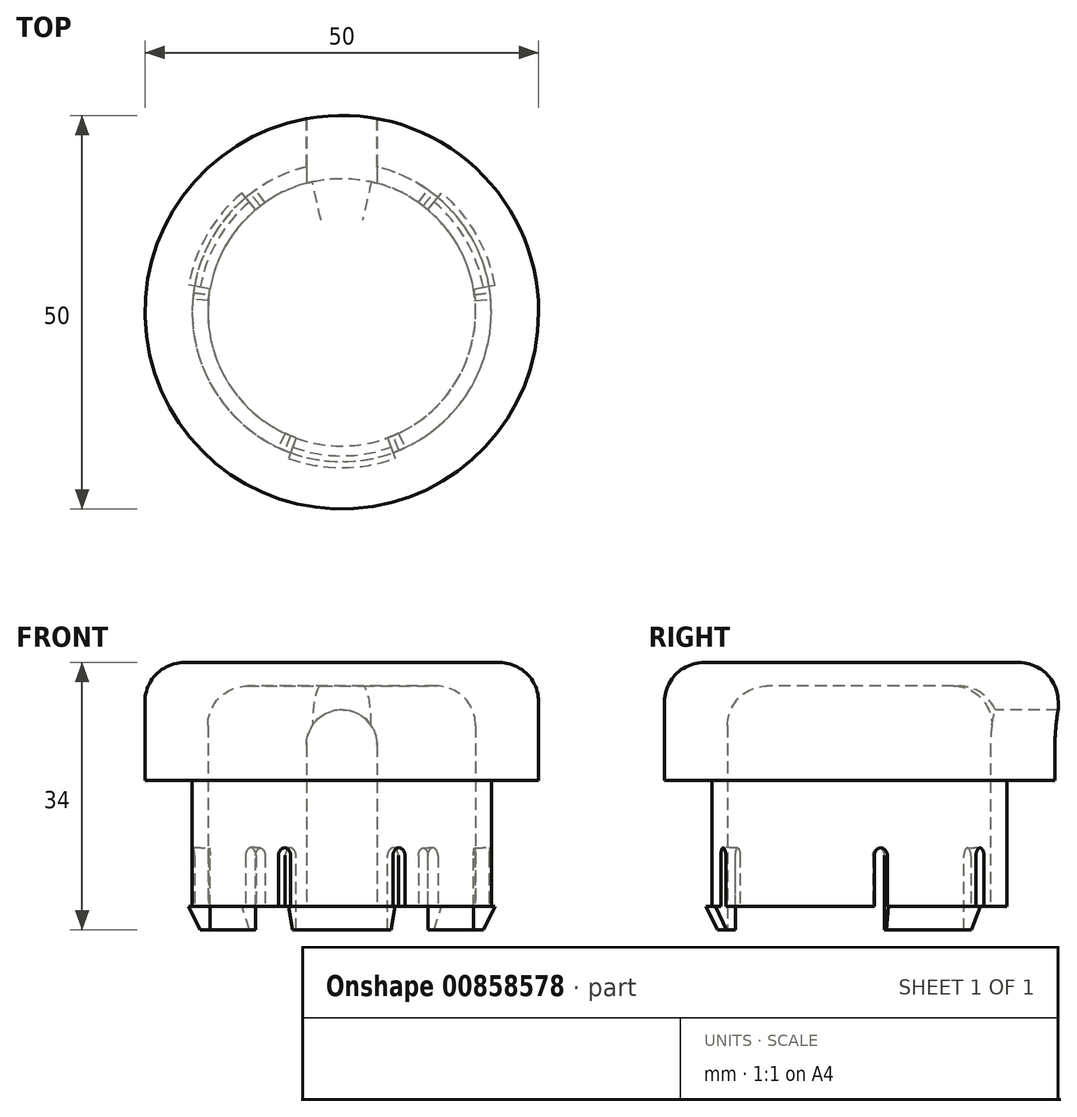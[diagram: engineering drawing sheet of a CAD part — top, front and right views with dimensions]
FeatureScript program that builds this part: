
annotation { "Feature Type Name" : "Feature", "Feature Type Description" : "" }
export const myFeature = defineFeature(function(context is Context, id is Id, definition is map)
    precondition{}
    {
        {
            var Q0;
            Q0=qCreatedBy(makeId("Top.planeOp"),FACE);
            var sketch = newSketch(context, id + "F0", { "sketchPlane" : qUnion([Q0])});
            skCircle(sketch, "E0", {"center": v(0, 0) * mm, "radius": 19 * mm});
            skSolve(sketch);
        }
        {
            var Q0;
            Q0 = qSketchRegion(id + "F0", true);
            extrude(context, id + "F1", {"entities" : qUnion([Q0]), "depth" : 16 * mm, "offsetDistance" : 25 * mm});
        }
        {
            var Q0;
            Q0=makeQuery(id+"F1.opExtrude","CAP_FACE",FACE,{"disambiguationData":[OSD([sQuery(id+"F0.wireOp",EDGE,"E0")])],"isStart":false});
            var sketch = newSketch(context, id + "F2", { "sketchPlane" : qUnion([Q0])});
            skCircle(sketch, "E1", {"center": v(0, 0) * mm, "radius": 25 * mm});
            skSolve(sketch);
        }
        {
            var Q0;
            Q0 = qSketchRegion(id + "F2", true);
            extrude(context, id + "F3", {"entities" : qUnion([Q0]), "operationType" : NewBodyOperationType.ADD, "depth" : 15 * mm, "offsetDistance" : 25 * mm});
        }
        {
            var Q0;
            Q0=makeQuery(id+"F1.opExtrude","CAP_FACE",FACE,{"disambiguationData":[OSD([sQuery(id+"F0.wireOp",EDGE,"E0")])],"isStart":true});
            var sketch = newSketch(context, id + "F4", { "sketchPlane" : qUnion([Q0])});
            skCircle(sketch, "E2", {"center": v(0, 0) * mm, "radius": 17 * mm});
            skSolve(sketch);
        }
        {
            var Q0;
            Q0 = qSketchRegion(id + "F4", true);
            extrude(context, id + "F5", {"entities" : qUnion([Q0]), "operationType" : NewBodyOperationType.REMOVE, "oppositeDirection" : true, "depth" : 28 * mm, "offsetDistance" : 25 * mm});
        }
        {
            var Q0;
            Q0=qCreatedBy(makeId("Front.planeOp"),FACE);
            var sketch = newSketch(context, id + "F6", { "sketchPlane" : qUnion([Q0])});
            skLineSegment(sketch, "E3", {"start": v(-4.5, 0) * mm, "end": v(-4.5, 20.5) * mm});
            skLineSegment(sketch, "E4", {"start": v(-8.7, 16) * mm, "end": v(8.8, 16) * mm});
            skLineSegment(sketch, "E5.0", {"start": v(-8.7, 25) * mm, "end": v(8.8, 25) * mm});
            skLineSegment(sketch, "E6.MirrorCS", {"start": v(4.5, 0) * mm, "end": v(4.5, 20.5) * mm});
            skArc(sketch, "E7", {"start": v(4.5, 20.5) * mm, "mid": v(0, 25) * mm, "end": v(-4.5, 20.5) * mm});
            skLineSegment(sketch, "E8", {"start": v(-4.5, 0) * mm, "end": v(4.5, 0) * mm});
            skSolve(sketch);
        }
        {
            var Q0;
            Q0 = qSketchRegion(id + "F6", true);
            extrude(context, id + "F7", {"entities" : qUnion([Q0]), "operationType" : NewBodyOperationType.REMOVE, "oppositeDirection" : true, "depth" : 25 * mm, "offsetDistance" : 25 * mm});
        }
        {
            var Q0;
            Q0=makeQuery(id+"F5.boolean.opBoolean","COPY",EDGE,{"derivedFrom":makeQuery(id+"F5.opExtrude","CAP_EDGE",EDGE,{"disambiguationData":[OSD([sQuery(id+"F4.wireOp",EDGE,"E2")])],"isStart":false})});
            fillet(context, id + "F8", {"entities" : qUnion([Q0]), "tangentPropagation" : true, "radius" : 5 * mm, "defaultsChanged" : false, "vertexSettings" : [], "allowEdgeOverflow" : false});
        }
        {
            var Q0;
            Q0=makeQuery(id+"F3.opExtrude","CAP_FACE",FACE,{"disambiguationData":[OSD([sQuery(id+"F2.wireOp",EDGE,"E1")])],"isStart":false});
            fillet(context, id + "F9", {"entities" : qUnion([Q0]), "tangentPropagation" : true, "radius" : 5 * mm, "defaultsChanged" : true, "vertexSettings" : [], "allowEdgeOverflow" : false});
        }
        {
            var Q0;
            Q0=makeQuery(id+"F1.opExtrude","CAP_FACE",FACE,{"disambiguationData":[OSD([sQuery(id+"F0.wireOp",EDGE,"E0")])],"isStart":true});
            var sketch = newSketch(context, id + "F10", { "sketchPlane" : qUnion([Q0])});
            skLineSegment(sketch, "E9", {"start": v(-5.81, 15.97) * mm, "end": v(-6.75, 18.56) * mm});
            skLineSegment(sketch, "E10.MirrorCS", {"start": v(5.81, 15.97) * mm, "end": v(6.75, 18.56) * mm});
            skArc(sketch, "E11", {"start": v(6.75, 18.56) * mm, "mid": v(0, 19.75) * mm, "end": v(-6.75, 18.56) * mm});
            skArc(sketch, "E12", {"start": v(5.81, 15.97) * mm, "mid": v(0, 17) * mm, "end": v(-5.81, 15.97) * mm});
            skArc(sketch, "E13.1.0", {"start": v(-19.45, -3.43) * mm, "mid": v(-17.1, -9.87) * mm, "end": v(-12.7, -15.13) * mm});
            skLineSegment(sketch, "E13.1.1", {"start": v(-10.93, -13.02) * mm, "end": v(-12.7, -15.13) * mm});
            skLineSegment(sketch, "E13.1.2", {"start": v(-16.74, -2.95) * mm, "end": v(-19.45, -3.43) * mm});
            skArc(sketch, "E13.1.3", {"start": v(-16.74, -2.95) * mm, "mid": v(-14.72, -8.5) * mm, "end": v(-10.93, -13.02) * mm});
            skArc(sketch, "E13.2.0", {"start": v(12.7, -15.13) * mm, "mid": v(17.1, -9.88) * mm, "end": v(19.45, -3.43) * mm});
            skLineSegment(sketch, "E13.2.1", {"start": v(16.74, -2.95) * mm, "end": v(19.45, -3.43) * mm});
            skLineSegment(sketch, "E13.2.2", {"start": v(10.93, -13.02) * mm, "end": v(12.7, -15.13) * mm});
            skArc(sketch, "E13.2.3", {"start": v(10.93, -13.02) * mm, "mid": v(14.72, -8.5) * mm, "end": v(16.74, -2.95) * mm});
            skSolve(sketch);
        }
        {
            var Q0;
            Q0 = qSketchRegion(id + "F10", true);
            extrude(context, id + "F11", {"entities" : qUnion([Q0]), "operationType" : NewBodyOperationType.ADD, "depth" : 3 * mm, "offsetDistance" : 25 * mm});
        }
        {
            var Q0;
            Q0=makeQuery(id+"F11.opExtrude","CAP_EDGE",EDGE,{"disambiguationData":[OSD([sQuery(id+"F10.wireOp",EDGE,"E13.1.0")])],"isStart":false});
            var Q1;
            Q1=makeQuery(id+"F11.opExtrude","CAP_EDGE",EDGE,{"disambiguationData":[OSD([sQuery(id+"F10.wireOp",EDGE,"E13.2.0")])],"isStart":false});
            var Q2;
            Q2=makeQuery(id+"F11.opExtrude","CAP_EDGE",EDGE,{"disambiguationData":[OSD([sQuery(id+"F10.wireOp",EDGE,"E11")])],"isStart":false});
            chamfer(context, id + "F12", {"entities" : qUnion([Q0, Q1, Q2]), "chamferType" : ChamferType.TWO_OFFSETS, "width1" : 1.5 * mm, "oppositeDirection" : false, "width2" : 3 * mm, "tangentPropagation" : true});
        }
        {
            var Q0;
            {var subQ0=sQuery(id+"F10.wireOp",EDGE,"E9");var subQ3=sQuery(id+"F0.wireOp",EDGE,"E0");Q0=makeQuery(id+"F11.boolean.opBoolean","SPLIT",FACE,{"disambiguationData":[TD([makeQuery(id+"F11.opExtrude","SWEPT_FACE",FACE,{"disambiguationData":[OSD([subQ0])]})])],"derivedFrom":makeQuery(id+"F1.opExtrude","CAP_FACE",FACE,{"disambiguationData":[OSD([subQ3])],"isStart":true})});}
            var sketch = newSketch(context, id + "F13", { "sketchPlane" : qUnion([Q0])});
            skLineSegment(sketch, "E14", {"start": v(-5.81, 15.97) * mm, "end": v(-6.5, 17.85) * mm});
            skLineSegment(sketch, "E15", {"start": v(-7.18, 15.4) * mm, "end": v(-8.03, 17.22) * mm});
            skArc(sketch, "E16", {"start": v(-5.81, 15.97) * mm, "mid": v(-6.5, 15.7) * mm, "end": v(-7.18, 15.4) * mm});
            skArc(sketch, "E17", {"start": v(-6.5, 17.85) * mm, "mid": v(-7.27, 17.55) * mm, "end": v(-8.03, 17.22) * mm});
            skArc(sketch, "E18.MirrorCS", {"start": v(5.81, 15.97) * mm, "mid": v(6.5, 15.7) * mm, "end": v(7.18, 15.4) * mm});
            skArc(sketch, "E19.MirrorCS", {"start": v(6.5, 17.85) * mm, "mid": v(7.27, 17.55) * mm, "end": v(8.03, 17.22) * mm});
            skLineSegment(sketch, "E20.MirrorCS", {"start": v(7.18, 15.4) * mm, "end": v(8.03, 17.22) * mm});
            skLineSegment(sketch, "E21.MirrorCS", {"start": v(5.81, 15.97) * mm, "end": v(6.5, 17.85) * mm});
            skLineSegment(sketch, "E22.1.0", {"start": v(-10.93, -13.02) * mm, "end": v(-12.21, -14.55) * mm});
            skLineSegment(sketch, "E22.1.1", {"start": v(-16.94, -1.48) * mm, "end": v(-18.93, -1.66) * mm});
            skLineSegment(sketch, "E22.1.2", {"start": v(-16.74, -2.95) * mm, "end": v(-18.71, -3.3) * mm});
            skLineSegment(sketch, "E22.1.3", {"start": v(-9.75, -13.93) * mm, "end": v(-10.9, -15.56) * mm});
            skArc(sketch, "E22.1.4", {"start": v(-10.93, -13.02) * mm, "mid": v(-10.35, -13.49) * mm, "end": v(-9.75, -13.93) * mm});
            skArc(sketch, "E22.1.5", {"start": v(-18.71, -3.3) * mm, "mid": v(-18.84, -2.48) * mm, "end": v(-18.93, -1.66) * mm});
            skArc(sketch, "E22.1.6", {"start": v(-12.21, -14.55) * mm, "mid": v(-11.57, -15.07) * mm, "end": v(-10.9, -15.56) * mm});
            skArc(sketch, "E22.1.7", {"start": v(-16.74, -2.95) * mm, "mid": v(-16.85, -2.22) * mm, "end": v(-16.94, -1.48) * mm});
            skLineSegment(sketch, "E22.2.0", {"start": v(16.74, -2.95) * mm, "end": v(18.71, -3.3) * mm});
            skLineSegment(sketch, "E22.2.1", {"start": v(9.75, -13.93) * mm, "end": v(10.9, -15.56) * mm});
            skLineSegment(sketch, "E22.2.2", {"start": v(10.93, -13.02) * mm, "end": v(12.21, -14.55) * mm});
            skLineSegment(sketch, "E22.2.3", {"start": v(16.94, -1.48) * mm, "end": v(18.93, -1.66) * mm});
            skArc(sketch, "E22.2.4", {"start": v(16.74, -2.95) * mm, "mid": v(16.85, -2.22) * mm, "end": v(16.94, -1.48) * mm});
            skArc(sketch, "E22.2.5", {"start": v(12.21, -14.55) * mm, "mid": v(11.57, -15.07) * mm, "end": v(10.9, -15.56) * mm});
            skArc(sketch, "E22.2.6", {"start": v(18.71, -3.3) * mm, "mid": v(18.84, -2.48) * mm, "end": v(18.93, -1.66) * mm});
            skArc(sketch, "E22.2.7", {"start": v(10.93, -13.02) * mm, "mid": v(10.35, -13.49) * mm, "end": v(9.75, -13.93) * mm});
            skSolve(sketch);
        }
        {
            var Q0;
            Q0 = qSketchRegion(id + "F13", true);
            extrude(context, id + "F14", {"entities" : qUnion([Q0]), "operationType" : NewBodyOperationType.REMOVE, "oppositeDirection" : true, "depth" : 7.5 * mm, "offsetDistance" : 25 * mm});
        }
        {
            var Q0;
            Q0=makeQuery(id+"F14.boolean.opBoolean","COPY",EDGE,{"derivedFrom":makeQuery(id+"F14.opExtrude","CAP_EDGE",EDGE,{"disambiguationData":[OSD([sQuery(id+"F13.wireOp",EDGE,"E22.2.2")])],"isStart":false})});
            var Q1;
            Q1=makeQuery(id+"F14.boolean.opBoolean","COPY",EDGE,{"derivedFrom":makeQuery(id+"F14.opExtrude","CAP_EDGE",EDGE,{"disambiguationData":[OSD([sQuery(id+"F13.wireOp",EDGE,"E22.2.1")])],"isStart":false})});
            var Q2;
            Q2=makeQuery(id+"F14.boolean.opBoolean","COPY",EDGE,{"derivedFrom":makeQuery(id+"F14.opExtrude","CAP_EDGE",EDGE,{"disambiguationData":[OSD([sQuery(id+"F13.wireOp",EDGE,"E22.2.0")])],"isStart":false})});
            var Q3;
            Q3=makeQuery(id+"F14.boolean.opBoolean","COPY",EDGE,{"derivedFrom":makeQuery(id+"F14.opExtrude","CAP_EDGE",EDGE,{"disambiguationData":[OSD([sQuery(id+"F13.wireOp",EDGE,"E22.2.3")])],"isStart":false})});
            var Q4;
            Q4=makeQuery(id+"F14.boolean.opBoolean","COPY",EDGE,{"derivedFrom":makeQuery(id+"F14.opExtrude","CAP_EDGE",EDGE,{"disambiguationData":[OSD([sQuery(id+"F13.wireOp",EDGE,"E20.MirrorCS")])],"isStart":false})});
            var Q5;
            Q5=makeQuery(id+"F14.boolean.opBoolean","COPY",EDGE,{"derivedFrom":makeQuery(id+"F14.opExtrude","CAP_EDGE",EDGE,{"disambiguationData":[OSD([sQuery(id+"F13.wireOp",EDGE,"E21.MirrorCS")])],"isStart":false})});
            var Q6;
            Q6=makeQuery(id+"F14.boolean.opBoolean","COPY",EDGE,{"derivedFrom":makeQuery(id+"F14.opExtrude","CAP_EDGE",EDGE,{"disambiguationData":[OSD([sQuery(id+"F13.wireOp",EDGE,"E14")])],"isStart":false})});
            var Q7;
            Q7=makeQuery(id+"F14.boolean.opBoolean","COPY",EDGE,{"derivedFrom":makeQuery(id+"F14.opExtrude","CAP_EDGE",EDGE,{"disambiguationData":[OSD([sQuery(id+"F13.wireOp",EDGE,"E15")])],"isStart":false})});
            var Q8;
            Q8=makeQuery(id+"F14.boolean.opBoolean","COPY",EDGE,{"derivedFrom":makeQuery(id+"F14.opExtrude","CAP_EDGE",EDGE,{"disambiguationData":[OSD([sQuery(id+"F13.wireOp",EDGE,"E22.1.1")])],"isStart":false})});
            var Q9;
            Q9=makeQuery(id+"F14.boolean.opBoolean","COPY",EDGE,{"derivedFrom":makeQuery(id+"F14.opExtrude","CAP_EDGE",EDGE,{"disambiguationData":[OSD([sQuery(id+"F13.wireOp",EDGE,"E22.1.2")])],"isStart":false})});
            var Q10;
            Q10=makeQuery(id+"F14.boolean.opBoolean","COPY",EDGE,{"derivedFrom":makeQuery(id+"F14.opExtrude","CAP_EDGE",EDGE,{"disambiguationData":[OSD([sQuery(id+"F13.wireOp",EDGE,"E22.1.0")])],"isStart":false})});
            var Q11;
            Q11=makeQuery(id+"F14.boolean.opBoolean","COPY",EDGE,{"derivedFrom":makeQuery(id+"F14.opExtrude","CAP_EDGE",EDGE,{"disambiguationData":[OSD([sQuery(id+"F13.wireOp",EDGE,"E22.1.3")])],"isStart":false})});
            fillet(context, id + "F15", {"entities" : qUnion([Q0, Q1, Q2, Q3, Q4, Q5, Q6, Q7, Q8, Q9, Q10, Q11]), "tangentPropagation" : true, "radius" : 1 * mm, "defaultsChanged" : false, "vertexSettings" : [], "allowEdgeOverflow" : false});
        }
    });
